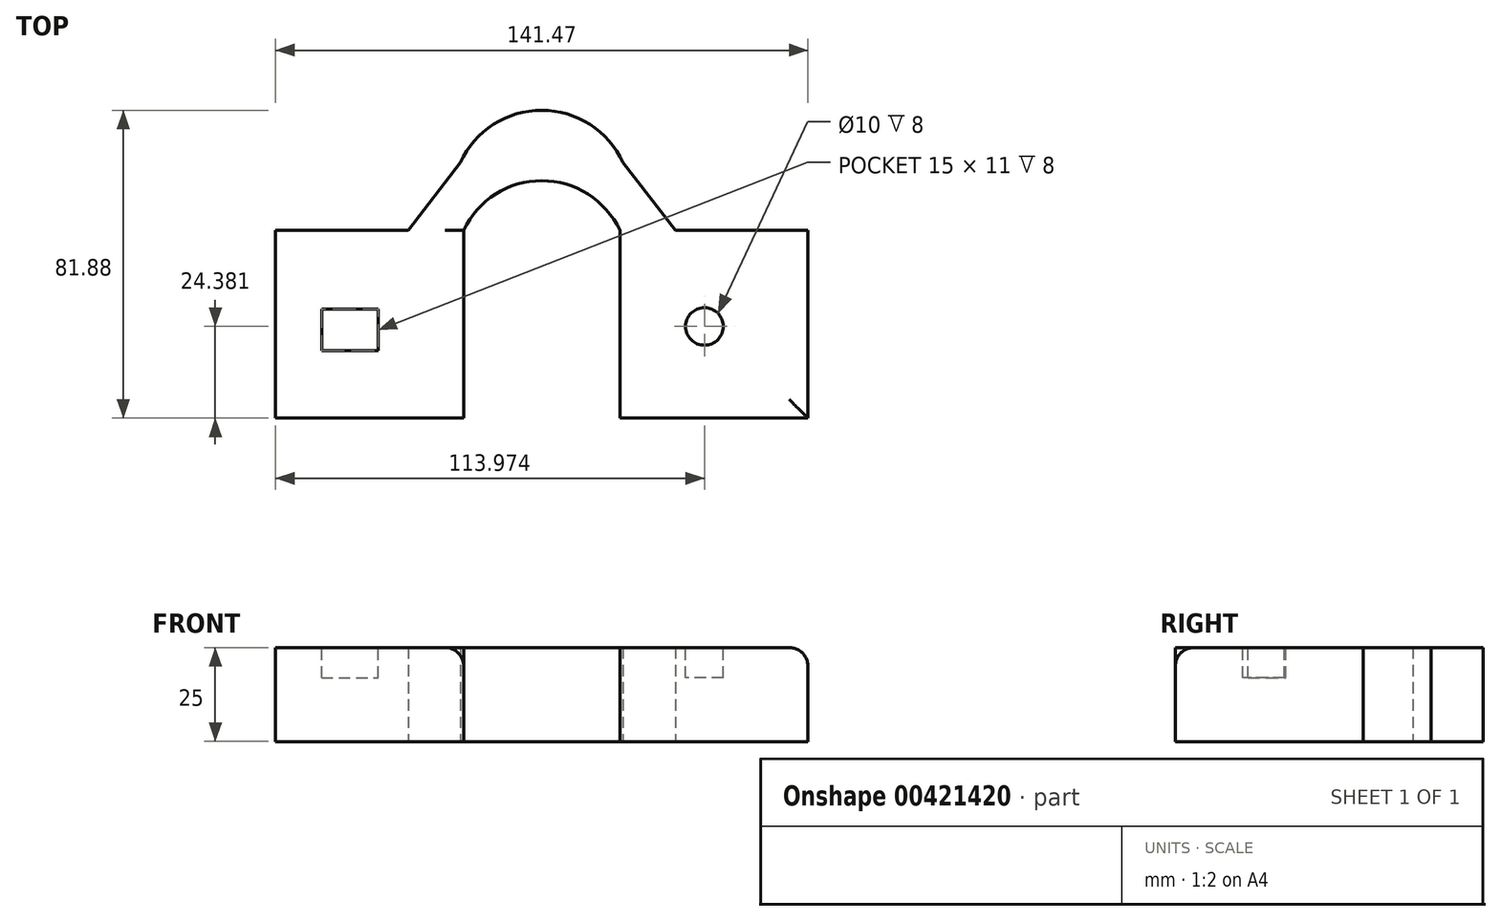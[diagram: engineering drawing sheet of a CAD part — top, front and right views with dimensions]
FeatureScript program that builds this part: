
annotation { "Feature Type Name" : "Feature", "Feature Type Description" : "" }
export const myFeature = defineFeature(function(context is Context, id is Id, definition is map)
    precondition{}
    {
        {
            var Q0;
            Q0=qCreatedBy(makeId("Front.planeOp"),FACE);
            var sketch = newSketch(context, id + "F0", { "sketchPlane" : qUnion([Q0])});
            skLineSegment(sketch, "E0.bottom", {"start": v(26.9, 32.97) * mm, "end": v(76.9, 32.97) * mm});
            skLineSegment(sketch, "E0.top", {"start": v(26.9, 57.97) * mm, "end": v(76.9, 57.97) * mm});
            skLineSegment(sketch, "E0.left", {"start": v(26.9, 32.97) * mm, "end": v(26.9, 57.97) * mm});
            skLineSegment(sketch, "E0.right", {"start": v(76.9, 32.97) * mm, "end": v(76.9, 57.97) * mm});
            skLineSegment(sketch, "E1", {"start": v(97.64, 32.97) * mm, "end": v(97.64, 69.36) * mm});
            skLineSegment(sketch, "E2.MirrorCS", {"start": v(168.37, 32.97) * mm, "end": v(118.37, 32.97) * mm});
            skLineSegment(sketch, "E3.MirrorCS", {"start": v(168.37, 57.97) * mm, "end": v(118.37, 57.97) * mm});
            skLineSegment(sketch, "E4.MirrorCS", {"start": v(168.37, 32.97) * mm, "end": v(168.37, 57.97) * mm});
            skLineSegment(sketch, "E5.MirrorCS", {"start": v(118.37, 32.97) * mm, "end": v(118.37, 57.97) * mm});
            skSolve(sketch);
        }
        {
            var Q0;
            Q0=makeQuery(id+"F0.imprint","IMPRINT",FACE,{"disambiguationData":[TD([[makeQuery(id+"F0.imprint","IMPRINT",EDGE,{"derivedFrom":sQuery(id+"F0.wireOp",EDGE,"E0.bottom")}),1.0]])]});
            var Q1;
            Q1=makeQuery(id+"F0.imprint","IMPRINT",FACE,{"disambiguationData":[TD([[makeQuery(id+"F0.imprint","IMPRINT",EDGE,{"derivedFrom":sQuery(id+"F0.wireOp",EDGE,"E2.MirrorCS")}),-1.0]])]});
            extrude(context, id + "F1", {"entities" : qUnion([Q0, Q1]), "depth" : 50 * mm});
        }
        {
            var Q0;
            Q0=makeQuery(id+"F1.opExtrude","SWEPT_EDGE",EDGE,{"disambiguationData":[OSD([sQuery(id+"F0.wireOp",EDGE,"E3.MirrorCS"),sQuery(id+"F0.wireOp",EDGE,"E4.MirrorCS")])]});
            var Q1;
            Q1=makeQuery(id+"F1.opExtrude","SWEPT_EDGE",EDGE,{"disambiguationData":[OSD([sQuery(id+"F0.wireOp",EDGE,"E0.top"),sQuery(id+"F0.wireOp",EDGE,"E0.right")])]});
            var Q2;
            Q2=makeQuery(id+"F1.opExtrude","CAP_EDGE",EDGE,{"disambiguationData":[OSD([sQuery(id+"F0.wireOp",EDGE,"E3.MirrorCS")])],"isStart":false});
            fillet(context, id + "F2", {"entities" : qUnion([Q0, Q1, Q2]), "radius" : 5 * mm, "tangentPropagation" : true, "allowEdgeOverflow" : false});
        }
        {
            var Q0;
            Q0=makeQuery(id+"F1.opExtrude","SWEPT_FACE",FACE,{"disambiguationData":[OSD([sQuery(id+"F0.wireOp",EDGE,"E3.MirrorCS")])]});
            var sketch = newSketch(context, id + "F3", { "sketchPlane" : qUnion([Q0])});
            skCircle(sketch, "E6", {"center": v(140.87, -25.62) * mm, "radius": 5 * mm});
            skPoint(sketch, "E6.centerSnap0", {"position": v(140.87, -45) * mm});
            skLineSegment(sketch, "E7.bottom", {"start": v(39.13, -21.05) * mm, "end": v(54.13, -21.05) * mm});
            skLineSegment(sketch, "E7.top", {"start": v(39.13, -32.05) * mm, "end": v(54.13, -32.05) * mm});
            skLineSegment(sketch, "E7.left", {"start": v(39.13, -21.05) * mm, "end": v(39.13, -32.05) * mm});
            skLineSegment(sketch, "E7.right", {"start": v(54.13, -21.05) * mm, "end": v(54.13, -32.05) * mm});
            skSolve(sketch);
        }
        {
            var Q0;
            Q0=makeQuery(id+"F3.imprint","IMPRINT",FACE,{"disambiguationData":[TD([[makeQuery(id+"F3.imprint","IMPRINT",EDGE,{"derivedFrom":sQuery(id+"F3.wireOp",EDGE,"E7.bottom")}),-1.0]])]});
            var Q1;
            Q1=makeQuery(id+"F3.imprint","IMPRINT",FACE,{"disambiguationData":[TD([[makeQuery(id+"F3.imprint","IMPRINT",EDGE,{"derivedFrom":sQuery(id+"F3.wireOp",EDGE,"E6")}),1.0]])]});
            extrude(context, id + "F4", {"entities" : qUnion([Q0, Q1]), "operationType" : NewBodyOperationType.REMOVE, "oppositeDirection" : true, "depth" : 8 * mm});
        }
        {
            var Q0;
            Q0=makeQuery(id+"F1.opExtrude","SWEPT_FACE",FACE,{"disambiguationData":[OSD([sQuery(id+"F0.wireOp",EDGE,"E2.MirrorCS")])]});
            cPlane(context, id + "F5", {"entities" : qUnion([Q0]), "cplaneType" : CPlaneType.OFFSET, "offset" : 0 * mm, "width" : 150 * mm, "height" : 150 * mm});
        }
        {
            var Q0;
            Q0=qCreatedBy(id+"F5.planeOp",FACE);
            var sketch = newSketch(context, id + "F6", { "sketchPlane" : qUnion([Q0])});
            skArc(sketch, "E8", {"start": v(76.9, 0) * mm, "mid": v(97.64, -13.13) * mm, "end": v(118.37, 0) * mm});
            skArc(sketch, "E9", {"start": v(76.05, -17.99) * mm, "mid": v(98.25, -31.88) * mm, "end": v(119.7, -16.86) * mm});
            skLineSegment(sketch, "E10", {"start": v(76.05, -17.99) * mm, "end": v(62.16, 0) * mm});
            skLineSegment(sketch, "E11", {"start": v(97.64, -40.11) * mm, "end": v(97.64, -51.07) * mm, "construction": true});
            skLineSegment(sketch, "E12.MirrorCS", {"start": v(119.22, -17.99) * mm, "end": v(133.1, 0) * mm});
            skLineSegment(sketch, "E13", {"start": v(62.16, 0) * mm, "end": v(76.9, 0) * mm});
            skLineSegment(sketch, "E14.MirrorCS", {"start": v(133.1, 0) * mm, "end": v(118.37, 0) * mm});
            skSolve(sketch);
        }
        {
            var Q0;
            Q0=makeQuery(id+"F6.imprint","IMPRINT",FACE,{"disambiguationData":[TD([[makeQuery(id+"F6.imprint","IMPRINT",EDGE,{"derivedFrom":sQuery(id+"F6.wireOp",EDGE,"E8")}),-1.0]])]});
            extrude(context, id + "F7", {"entities" : qUnion([Q0]), "operationType" : NewBodyOperationType.ADD, "oppositeDirection" : true, "depth" : 25 * mm});
        }
    });
